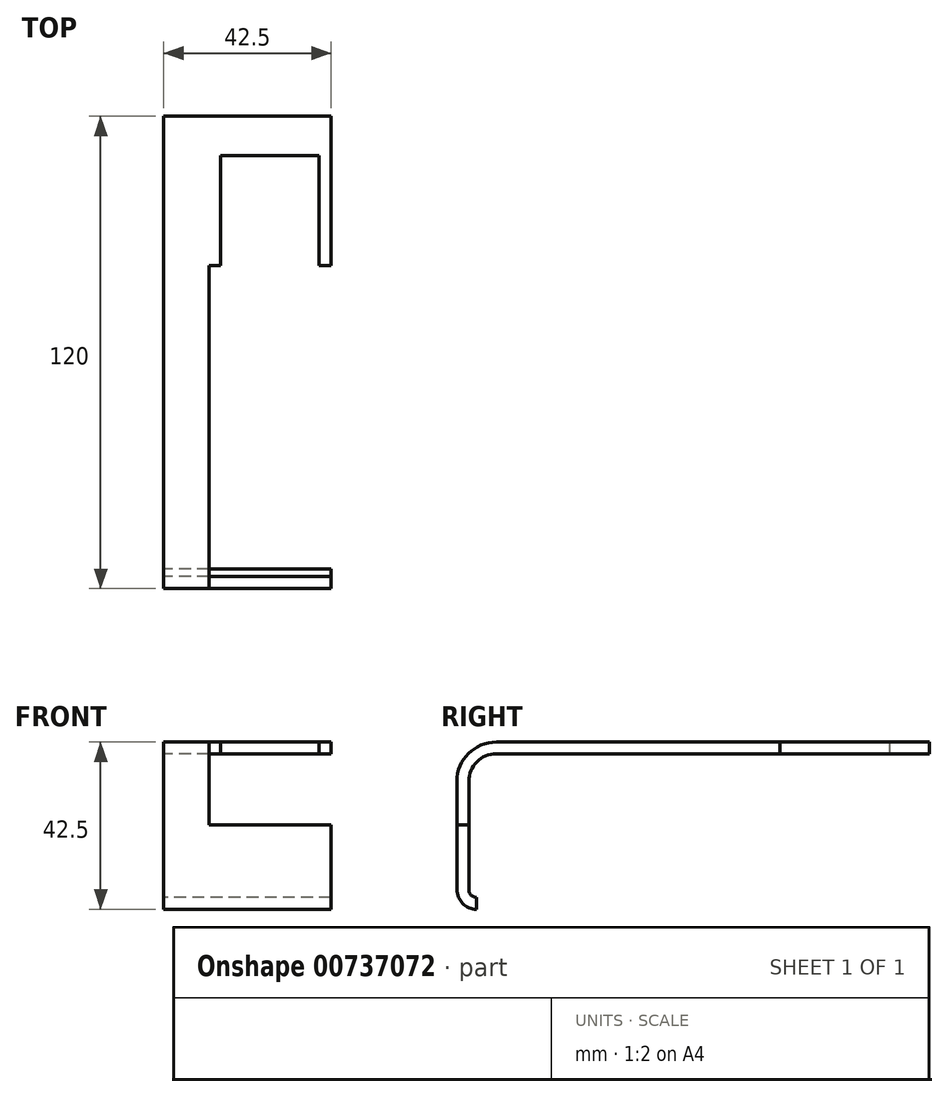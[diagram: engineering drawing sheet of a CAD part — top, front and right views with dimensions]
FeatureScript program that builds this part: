
annotation { "Feature Type Name" : "Feature", "Feature Type Description" : "" }
export const myFeature = defineFeature(function(context is Context, id is Id, definition is map)
    precondition{}
    {
        {
            var Q0;
            Q0=qCreatedBy(makeId("Right.planeOp"),FACE);
            var sketch = newSketch(context, id + "F0", { "sketchPlane" : qUnion([Q0])});
            skLineSegment(sketch, "E0", {"start": v(120, 0) * mm, "end": v(10, 0) * mm});
            skLineSegment(sketch, "E1", {"start": v(0, -10) * mm, "end": v(0, -37.5) * mm});
            skPoint(sketch, "E2.visualSharp", {"position": v(0, 0) * mm});
            skArc(sketch, "E2.filletArc", {"start": v(10, 0) * mm, "mid": v(2.93, -2.93) * mm, "end": v(0, -10) * mm});
            skPoint(sketch, "E3.visualSharp", {"position": v(0, -43) * mm});
            skArc(sketch, "E3.filletArc", {"start": v(0, -37.5) * mm, "mid": v(1.46, -41.04) * mm, "end": v(5, -42.5) * mm});
            skArc(sketch, "E4.0", {"start": v(3, -37.5) * mm, "mid": v(3.59, -38.91) * mm, "end": v(5, -39.5) * mm});
            skLineSegment(sketch, "E5.0", {"start": v(3, -10) * mm, "end": v(3, -37.5) * mm});
            skArc(sketch, "E6.0", {"start": v(10, -3) * mm, "mid": v(5.05, -5.05) * mm, "end": v(3, -10) * mm});
            skLineSegment(sketch, "E7.0", {"start": v(120, -3) * mm, "end": v(10, -3) * mm});
            skLineSegment(sketch, "E8", {"start": v(120, 0) * mm, "end": v(120, -3) * mm});
            skLineSegment(sketch, "E9", {"start": v(5, -39.5) * mm, "end": v(5, -42.5) * mm});
            skSolve(sketch);
        }
        {
            var Q0;
            Q0 = qSketchRegion(id + "F0", true);
            extrude(context, id + "F1", {"entities" : qUnion([Q0]), "depth" : 42.5 * mm, "offsetDistance" : 25 * mm});
        }
        {
            var Q0;
            Q0=makeQuery(id+"F1.opExtrude","SWEPT_FACE",FACE,{"disambiguationData":[OSD([sQuery(id+"F0.wireOp",EDGE,"E1")])]});
            var sketch = newSketch(context, id + "F2", { "sketchPlane" : qUnion([Q0])});
            skLineSegment(sketch, "E10.bottom", {"start": v(14.5, -21) * mm, "end": v(39.5, -21) * mm});
            skLineSegment(sketch, "E10.top", {"start": v(14.5, 0) * mm, "end": v(39.5, 0) * mm});
            skLineSegment(sketch, "E10.left", {"start": v(14.5, -21) * mm, "end": v(14.5, 0) * mm});
            skLineSegment(sketch, "E10.right", {"start": v(39.5, -21) * mm, "end": v(39.5, 0) * mm});
            skSolve(sketch);
        }
        {
            var Q0;
            Q0 = qSketchRegion(id + "F2", true);
            extrude(context, id + "F3", {"entities" : qUnion([Q0]), "operationType" : NewBodyOperationType.REMOVE, "oppositeDirection" : true, "depth" : 110 * mm, "offsetDistance" : 25 * mm});
        }
        {
            var Q0;
            Q0=makeQuery(id+"F1.opExtrude","SWEPT_FACE",FACE,{"disambiguationData":[OSD([sQuery(id+"F0.wireOp",EDGE,"E1")])]});
            var sketch = newSketch(context, id + "F4", { "sketchPlane" : qUnion([Q0])});
            skLineSegment(sketch, "E11.bottom", {"start": v(14.5, -21) * mm, "end": v(11.5, -21) * mm});
            skLineSegment(sketch, "E11.top", {"start": v(14.5, 0) * mm, "end": v(11.5, 0) * mm});
            skLineSegment(sketch, "E11.left", {"start": v(14.5, -21) * mm, "end": v(14.5, 0) * mm});
            skLineSegment(sketch, "E11.right", {"start": v(11.5, -21) * mm, "end": v(11.5, 0) * mm});
            skSolve(sketch);
        }
        {
            var Q0;
            Q0 = qSketchRegion(id + "F4", true);
            extrude(context, id + "F5", {"entities" : qUnion([Q0]), "operationType" : NewBodyOperationType.REMOVE, "oppositeDirection" : true, "depth" : 82 * mm, "offsetDistance" : 25 * mm});
        }
        {
            var Q0;
            Q0=makeQuery(id+"F1.opExtrude","SWEPT_FACE",FACE,{"disambiguationData":[OSD([sQuery(id+"F0.wireOp",EDGE,"E1")])]});
            var sketch = newSketch(context, id + "F6", { "sketchPlane" : qUnion([Q0])});
            skLineSegment(sketch, "E12.bottom", {"start": v(39.5, -21) * mm, "end": v(42.5, -21) * mm});
            skLineSegment(sketch, "E12.top", {"start": v(39.5, 0) * mm, "end": v(42.5, 0) * mm});
            skLineSegment(sketch, "E12.left", {"start": v(39.5, -21) * mm, "end": v(39.5, 0) * mm});
            skLineSegment(sketch, "E12.right", {"start": v(42.5, -21) * mm, "end": v(42.5, 0) * mm});
            skSolve(sketch);
        }
        {
            var Q0;
            Q0 = qSketchRegion(id + "F6", true);
            extrude(context, id + "F7", {"entities" : qUnion([Q0]), "operationType" : NewBodyOperationType.REMOVE, "oppositeDirection" : true, "depth" : 82 * mm, "offsetDistance" : 25 * mm});
        }
    });
